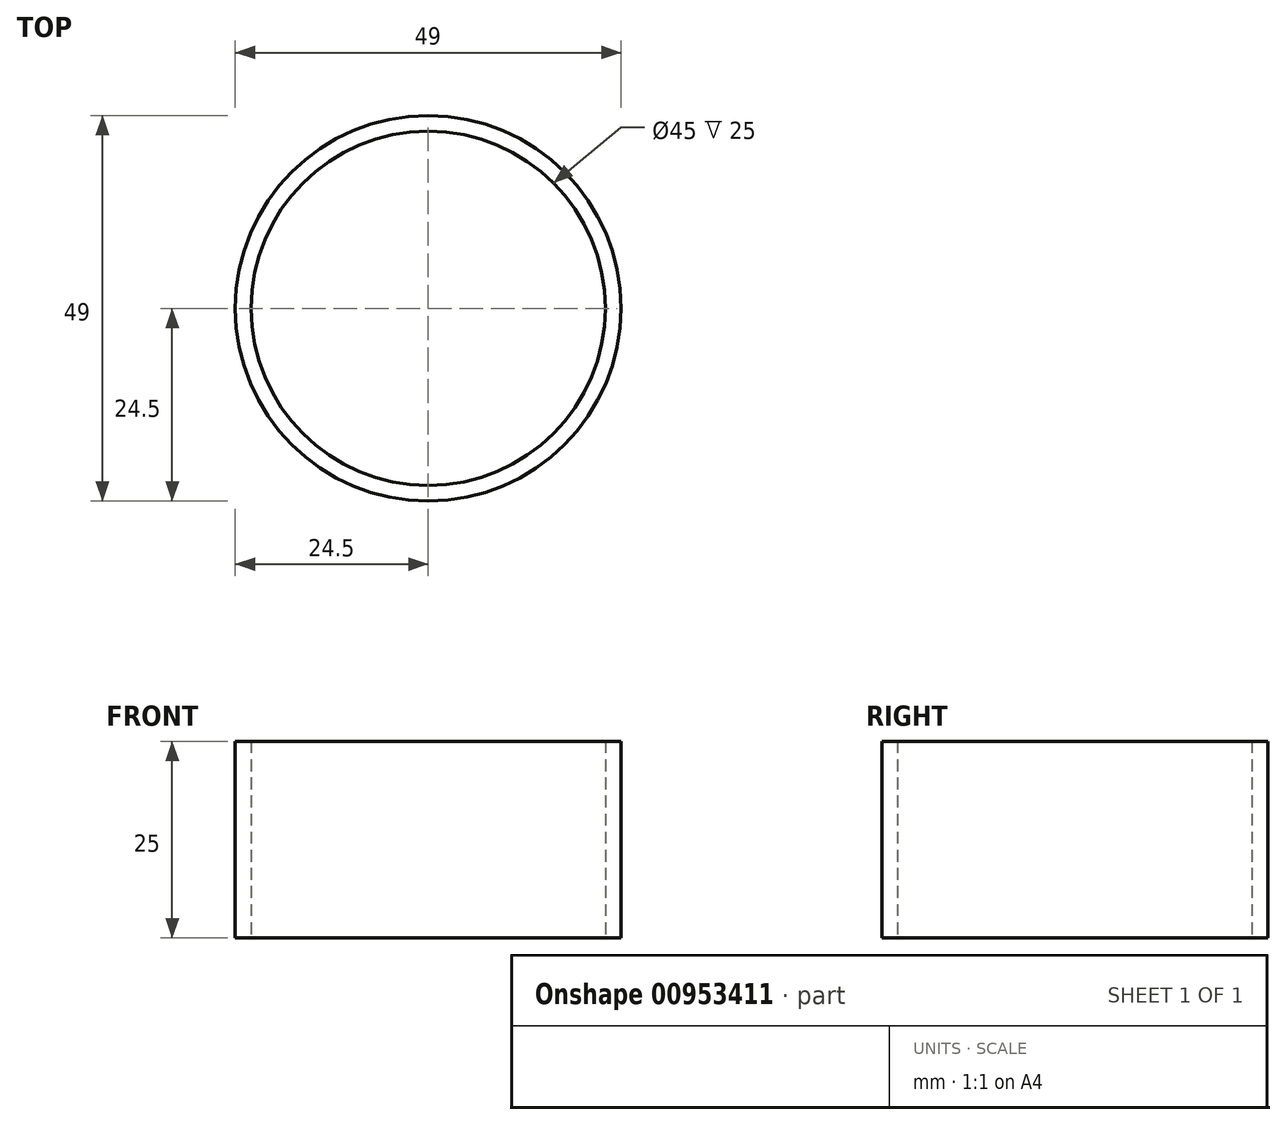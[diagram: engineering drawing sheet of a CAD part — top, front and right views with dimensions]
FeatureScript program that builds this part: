
annotation { "Feature Type Name" : "Feature", "Feature Type Description" : "" }
export const myFeature = defineFeature(function(context is Context, id is Id, definition is map)
    precondition{}
    {
        {
            var Q0;
            Q0=qCreatedBy(makeId("Top.planeOp"),FACE);
            var sketch = newSketch(context, id + "F0", { "sketchPlane" : qUnion([Q0])});
            skCircle(sketch, "E0", {"center": v(0, 0) * mm, "radius": 22.5 * mm});
            skCircle(sketch, "E1.0", {"center": v(0, 0) * mm, "radius": 24.5 * mm});
            skSolve(sketch);
        }
        {
            var Q0;
            Q0 = qSketchRegion(id + "F0", true);
            extrude(context, id + "F1", {"entities" : qUnion([Q0]), "depth" : 25 * mm, "offsetDistance" : 25 * mm});
        }
    });
